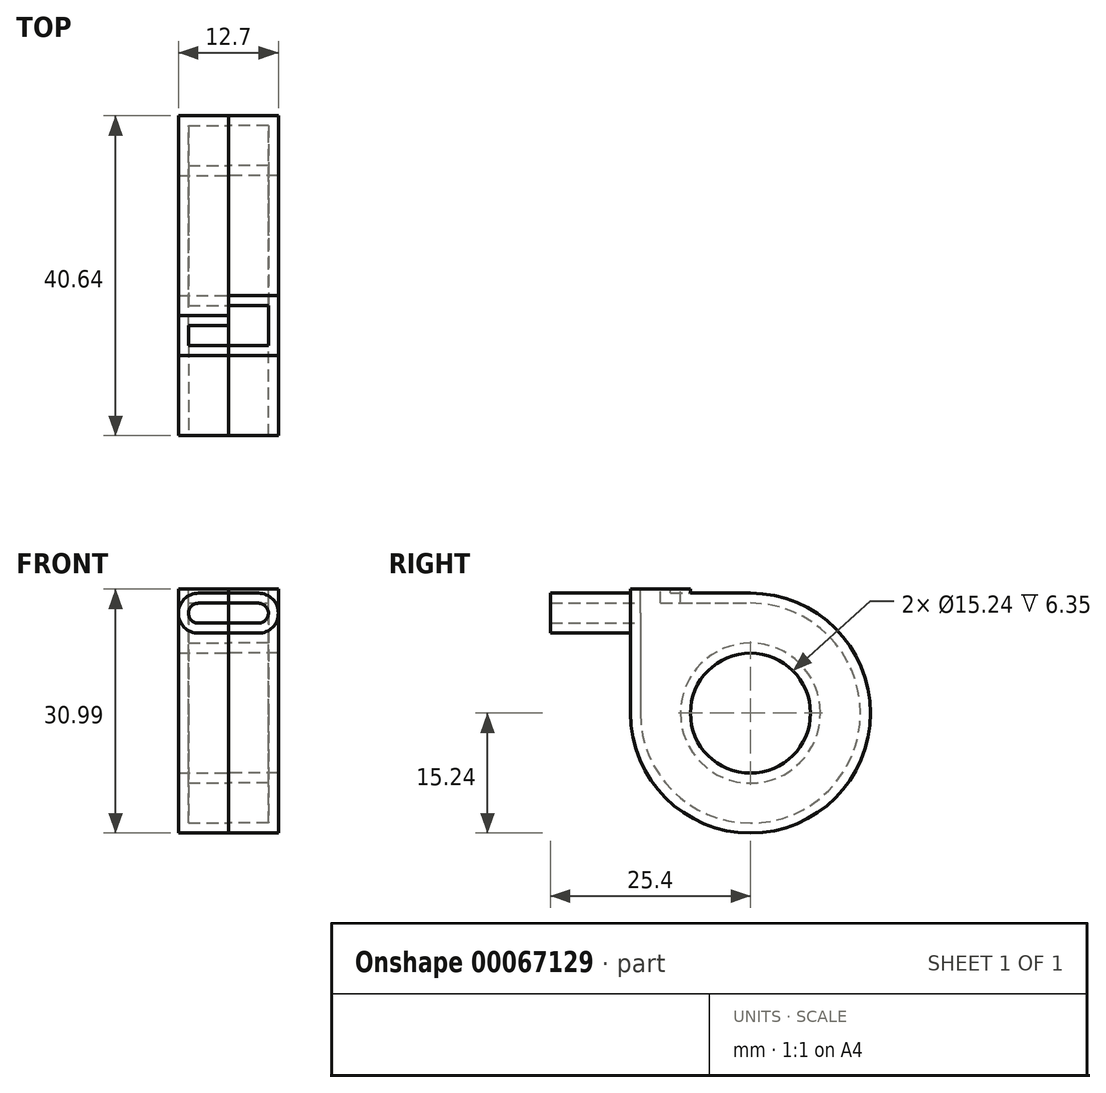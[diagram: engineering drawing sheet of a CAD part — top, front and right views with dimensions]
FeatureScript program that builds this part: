
annotation { "Feature Type Name" : "Feature", "Feature Type Description" : "" }
export const myFeature = defineFeature(function(context is Context, id is Id, definition is map)
    precondition{}
    {
        {
            var Q0;
            Q0=qCreatedBy(makeId("Right.planeOp"),FACE);
            var sketch = newSketch(context, id + "F0", { "sketchPlane" : qUnion([Q0])});
            skLineSegment(sketch, "E0", {"start": v(-25.4, 15.24) * mm, "end": v(0, 15.24) * mm});
            skArc(sketch, "E1", {"start": v(-15.24, 0) * mm, "mid": v(10.78, -10.78) * mm, "end": v(0, 15.24) * mm});
            skLineSegment(sketch, "E2", {"start": v(-25.4, 15.24) * mm, "end": v(-25.4, 10.16) * mm});
            skLineSegment(sketch, "E3", {"start": v(-25.4, 10.16) * mm, "end": v(-15.24, 10.16) * mm});
            skLineSegment(sketch, "E4", {"start": v(-15.24, 10.16) * mm, "end": v(-15.24, 0) * mm});
            skLineSegment(sketch, "E5.top", {"start": v(-15.24, 15.75) * mm, "end": v(-10.16, 15.75) * mm});
            skLineSegment(sketch, "E5.left", {"start": v(-15.24, 15.24) * mm, "end": v(-15.24, 15.75) * mm});
            skLineSegment(sketch, "E5.right", {"start": v(-10.16, 15.24) * mm, "end": v(-10.16, 15.75) * mm});
            skCircle(sketch, "E6", {"center": v(0, 0) * mm, "radius": 7.62 * mm});
            skSolve(sketch);
        }
        {
            var Q0;
            Q0=qSketchRegion(id+"F0",true);
            extrude(context, id + "F1", {"entities" : qUnion([Q0]), "oppositeDirection" : true, "depth" : 6.35 * mm});
        }
        {
            var Q0;
            Q0=makeQuery(id+"F1.opExtrude","SWEPT_FACE",FACE,{"disambiguationData":[OSD([sQuery(id+"F0.wireOp",EDGE,"E2")])]});
            var Q1;
            Q1=makeQuery(id+"F1.opExtrude","SWEPT_FACE",FACE,{"disambiguationData":[OSD([sQuery(id+"F0.wireOp",EDGE,"E5.top")])]});
            var Q2;
            Q2=makeQuery(id+"F1.opExtrude","CAP_FACE",FACE,{"disambiguationData":[OSD([sQuery(id+"F0.wireOp",EDGE,"E0"),sQuery(id+"F0.wireOp",EDGE,"E1"),sQuery(id+"F0.wireOp",EDGE,"E2"),sQuery(id+"F0.wireOp",EDGE,"E3"),sQuery(id+"F0.wireOp",EDGE,"E4"),sQuery(id+"F0.wireOp",EDGE,"E5.top"),sQuery(id+"F0.wireOp",EDGE,"E5.left"),sQuery(id+"F0.wireOp",EDGE,"E5.right"),sQuery(id+"F0.wireOp",EDGE,"E6")])],"isStart":true});
            shell(context, id + "F2", {"entities" : qUnion([Q0, Q1, Q2]), "thickness" : 1.27 * mm});
        }
        {
            var Q0;
            Q0=qCreatedBy(makeId("Right.planeOp"),FACE);
            var sketch = newSketch(context, id + "F3", { "sketchPlane" : qUnion([Q0])});
            skLineSegment(sketch, "E7", {"start": v(-25.4, 15.24) * mm, "end": v(0, 15.24) * mm});
            skArc(sketch, "E8", {"start": v(-15.24, 0) * mm, "mid": v(10.78, -10.78) * mm, "end": v(0, 15.24) * mm});
            skLineSegment(sketch, "E9", {"start": v(-25.4, 15.24) * mm, "end": v(-25.4, 10.16) * mm});
            skLineSegment(sketch, "E10", {"start": v(-25.4, 10.16) * mm, "end": v(-15.24, 10.16) * mm});
            skLineSegment(sketch, "E11", {"start": v(-15.24, 10.16) * mm, "end": v(-15.24, 0) * mm});
            skLineSegment(sketch, "E12.top", {"start": v(-15.24, 15.75) * mm, "end": v(-7.62, 15.75) * mm});
            skLineSegment(sketch, "E12.left", {"start": v(-15.24, 15.24) * mm, "end": v(-15.24, 15.75) * mm});
            skLineSegment(sketch, "E12.right", {"start": v(-7.62, 15.24) * mm, "end": v(-7.62, 15.75) * mm});
            skCircle(sketch, "E13", {"center": v(0, 0) * mm, "radius": 7.62 * mm});
            skSolve(sketch);
        }
        {
            var Q0;
            Q0 = qSketchRegion(id + "F3", true);
            extrude(context, id + "F4", {"entities" : qUnion([Q0]), "depth" : 6.35 * mm});
        }
        {
            var Q0;
            Q0=makeQuery(id+"F4.opExtrude","SWEPT_FACE",FACE,{"disambiguationData":[OSD([sQuery(id+"F3.wireOp",EDGE,"E9")])]});
            var Q1;
            Q1=makeQuery(id+"F4.opExtrude","SWEPT_FACE",FACE,{"disambiguationData":[OSD([sQuery(id+"F3.wireOp",EDGE,"E12.top")])]});
            var Q2;
            Q2=makeQuery(id+"F4.opExtrude","CAP_FACE",FACE,{"disambiguationData":[OSD([sQuery(id+"F3.wireOp",EDGE,"E7"),sQuery(id+"F3.wireOp",EDGE,"E8"),sQuery(id+"F3.wireOp",EDGE,"E9"),sQuery(id+"F3.wireOp",EDGE,"E10"),sQuery(id+"F3.wireOp",EDGE,"E11"),sQuery(id+"F3.wireOp",EDGE,"E12.top"),sQuery(id+"F3.wireOp",EDGE,"E12.left"),sQuery(id+"F3.wireOp",EDGE,"E12.right"),sQuery(id+"F3.wireOp",EDGE,"E13")])],"isStart":true});
            shell(context, id + "F5", {"entities" : qUnion([Q0, Q1, Q2]), "thickness" : 1.27 * mm});
        }
        {
            var Q0;
            {var subQ0=sQuery(id+"F0.wireOp",EDGE,"E0");Q0=makeQuery(id+"F1.opExtrude","CAP_EDGE",EDGE,{"disambiguationData":[OSD([subQ0]),TDD([makeQuery(id+"F0.imprint","IMPRINT",EDGE,{"disambiguationData":[TD([[makeQuery(id+"F0.imprint","INTERSECT",VERTEX,{"derivedFrom":[subQ0,sQuery(id+"F0.wireOp",EDGE,"E2")]}),-1.0]])],"derivedFrom":subQ0})])],"isStart":false});}
            var Q1;
            Q1=makeQuery(id+"F1.opExtrude","CAP_EDGE",EDGE,{"disambiguationData":[OSD([sQuery(id+"F0.wireOp",EDGE,"E3")])],"isStart":false});
            var Q2;
            {var subQ0=sQuery(id+"F3.wireOp",EDGE,"E7");Q2=makeQuery(id+"F4.opExtrude","CAP_EDGE",EDGE,{"disambiguationData":[OSD([subQ0]),TDD([makeQuery(id+"F3.imprint","IMPRINT",EDGE,{"disambiguationData":[TD([[makeQuery(id+"F3.imprint","INTERSECT",VERTEX,{"derivedFrom":[subQ0,sQuery(id+"F3.wireOp",EDGE,"E9")]}),-1.0]])],"derivedFrom":subQ0})])],"isStart":false});}
            var Q3;
            Q3=makeQuery(id+"F4.opExtrude","CAP_EDGE",EDGE,{"disambiguationData":[OSD([sQuery(id+"F3.wireOp",EDGE,"E10")])],"isStart":false});
            fillet(context, id + "F6", {"entities" : qUnion([Q0, Q1, Q2, Q3]), "radius" : 2.54 * mm, "tangentPropagation" : true, "allowEdgeOverflow" : false});
        }
        {
            var Q0;
            {var subQ0=sQuery(id+"F0.wireOp",EDGE,"E0");Q0=makeQuery(id+"F2.opShell","OFFSET_EDGE",EDGE,{"disambiguationData":[OSD([subQ0]),TDD([makeQuery(id+"F1.opExtrude","CAP_EDGE",EDGE,{"disambiguationData":[OSD([subQ0]),TDD([makeQuery(id+"F0.imprint","IMPRINT",EDGE,{"disambiguationData":[TD([[makeQuery(id+"F0.imprint","INTERSECT",VERTEX,{"derivedFrom":[subQ0,sQuery(id+"F0.wireOp",EDGE,"E2")]}),-1.0]])],"derivedFrom":subQ0})])],"isStart":false})])]});}
            var Q1;
            {var subQ0=sQuery(id+"F0.wireOp",EDGE,"E3");Q1=makeQuery(id+"F2.opShell","OFFSET_EDGE",EDGE,{"disambiguationData":[OSD([subQ0]),TDD([makeQuery(id+"F1.opExtrude","CAP_EDGE",EDGE,{"disambiguationData":[OSD([subQ0])],"isStart":false})])]});}
            var Q2;
            {var subQ0=sQuery(id+"F3.wireOp",EDGE,"E10");Q2=makeQuery(id+"F5.opShell","OFFSET_EDGE",EDGE,{"disambiguationData":[OSD([subQ0]),TDD([makeQuery(id+"F4.opExtrude","CAP_EDGE",EDGE,{"disambiguationData":[OSD([subQ0])],"isStart":false})])]});}
            var Q3;
            {var subQ0=sQuery(id+"F3.wireOp",EDGE,"E7");Q3=makeQuery(id+"F5.opShell","OFFSET_EDGE",EDGE,{"disambiguationData":[OSD([subQ0]),TDD([makeQuery(id+"F4.opExtrude","CAP_EDGE",EDGE,{"disambiguationData":[OSD([subQ0]),TDD([makeQuery(id+"F3.imprint","IMPRINT",EDGE,{"disambiguationData":[TD([[makeQuery(id+"F3.imprint","INTERSECT",VERTEX,{"derivedFrom":[subQ0,sQuery(id+"F3.wireOp",EDGE,"E9")]}),-1.0]])],"derivedFrom":subQ0})])],"isStart":false})])]});}
            fillet(context, id + "F7", {"entities" : qUnion([Q0, Q1, Q2, Q3]), "radius" : 1.27 * mm, "tangentPropagation" : true, "allowEdgeOverflow" : false});
        }
    });
